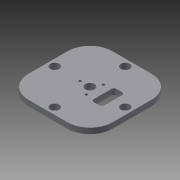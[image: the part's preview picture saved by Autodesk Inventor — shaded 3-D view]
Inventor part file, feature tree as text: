
AUTODESK INVENTOR PART (.ipt)
format: ipt  version: 2015 (Build 190159000, 159)  size: 138,752 bytes
history: native  units: in
note: dims shown in document units (in); Inventor stores cm internally (conversion verified against a paired STEP export)
features: extrude x2, fillet x2, sketch x2
ambient origin geometry x8: Origin, YZ Plane, XZ Plane, XY Plane, X Axis, Y Axis, Z Axis, Center Point
bodies: Body1 (feature_tree)
feature tree (6):
  extrude  "Extrusion6"  TaperAngle=120.0deg  [1 undecoded]
  fillet  "Fillet1"  Radius=0.4375in
  extrude  "Extrusion7"  Depth=0.4375in
  fillet  "Fillet2"  Radius=0.1174in
  sketch  "Sketch3"  dims[d19=120.0deg d20=120.0deg d21=0.4375in]
  sketch  "Sketch4"  dims[d22=0.4375in d23=0.4375in d24=0.1174in d25=0.1174in d26=0.1174in d27=3.1496in d28=3.1496in d29=0.3976in d30=0.3976in d31=3.75in d32=3.75in d33=0.25in d34=0.0in d35=1.0in d36=0.4134in d39=0.476in d40=1.024in d41=0.8in d42=1.0in d43=0.0in d44=0.125in]
note: 1 required parameter value undecoded (feature->parameter linkage not recoverable at this tier; creation-order binding heuristic only, values carry confidence <= 0.55)
